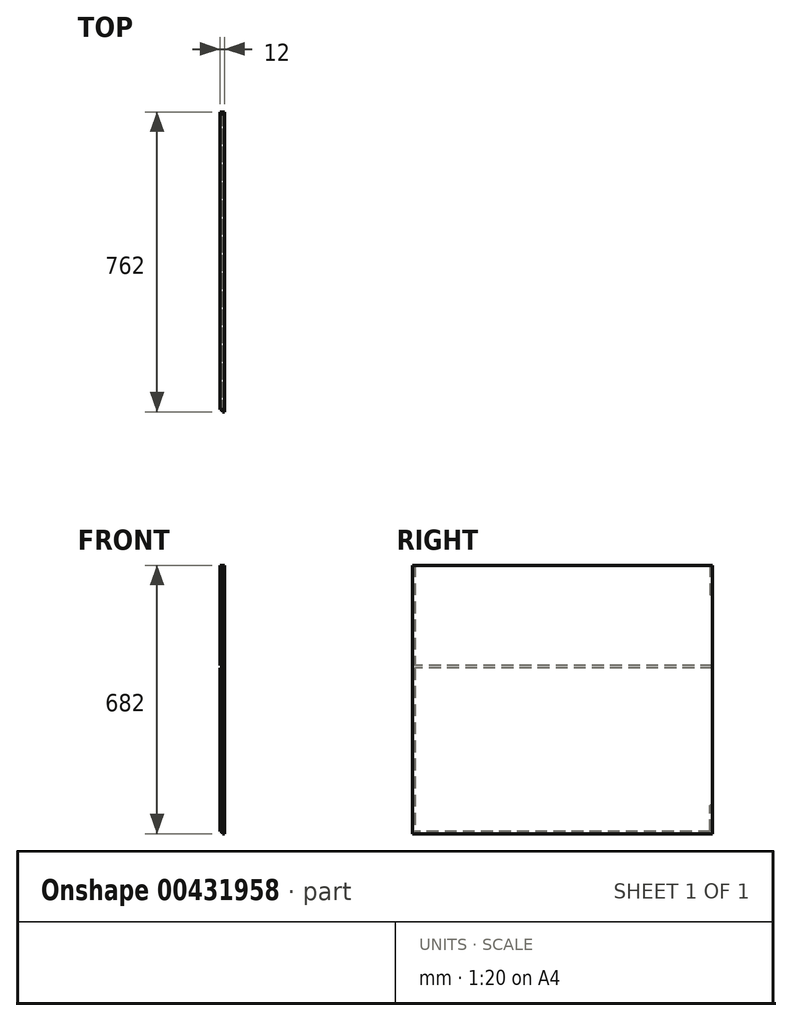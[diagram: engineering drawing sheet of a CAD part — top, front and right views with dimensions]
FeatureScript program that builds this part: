
annotation { "Feature Type Name" : "Feature", "Feature Type Description" : "" }
export const myFeature = defineFeature(function(context is Context, id is Id, definition is map)
    precondition{}
    {
        {
            var Q0;
            Q0=qCreatedBy(makeId("Right.planeOp"),FACE);
            var sketch = newSketch(context, id + "F0", { "sketchPlane" : qUnion([Q0])});
            skLineSegment(sketch, "E0.bottom", {"start": v(-381, 341) * mm, "end": v(381, 341) * mm});
            skLineSegment(sketch, "E0.top", {"start": v(-381, -341) * mm, "end": v(381, -341) * mm});
            skLineSegment(sketch, "E0.left", {"start": v(-381, 341) * mm, "end": v(-381, -341) * mm});
            skLineSegment(sketch, "E0.right", {"start": v(381, 341) * mm, "end": v(381, -341) * mm});
            skPoint(sketch, "E0.middle", {"position": v(0, 0) * mm});
            skSolve(sketch);
        }
        {
            var Q0;
            Q0=makeQuery(id+"F0.imprint","IMPRINT",FACE,{"disambiguationData":[TD([[makeQuery(id+"F0.imprint","IMPRINT",EDGE,{"derivedFrom":sQuery(id+"F0.wireOp",EDGE,"E0.bottom")}),-1.0]])]});
            extrude(context, id + "F1", {"entities" : qUnion([Q0]), "depth" : 12 * mm, "offsetDistance" : 25 * mm});
        }
        {
            var Q0;
            Q0=makeQuery(id+"F1.opExtrude","CAP_FACE",FACE,{"disambiguationData":[OSD([sQuery(id+"F0.wireOp",EDGE,"E0.bottom"),sQuery(id+"F0.wireOp",EDGE,"E0.top"),sQuery(id+"F0.wireOp",EDGE,"E0.left"),sQuery(id+"F0.wireOp",EDGE,"E0.right")])],"isStart":true});
            var sketch = newSketch(context, id + "F2", { "sketchPlane" : qUnion([Q0])});
            skLineSegment(sketch, "E1.bottom", {"start": v(381, 341) * mm, "end": v(375, 341) * mm});
            skLineSegment(sketch, "E1.top", {"start": v(381, -341) * mm, "end": v(375, -341) * mm});
            skLineSegment(sketch, "E1.left", {"start": v(381, 341) * mm, "end": v(381, -341) * mm});
            skLineSegment(sketch, "E1.right", {"start": v(375, 341) * mm, "end": v(375, -341) * mm});
            skSolve(sketch);
        }
        {
            var Q0;
            Q0=qSketchRegion(id+"F2",true);
            extrude(context, id + "F3", {"entities" : qUnion([Q0]), "operationType" : NewBodyOperationType.REMOVE, "oppositeDirection" : true, "depth" : 6 * mm, "offsetDistance" : 25 * mm});
        }
        {
            var Q0;
            {var subQ0=sQuery(id+"F0.wireOp",EDGE,"E0.bottom");var subQ1=sQuery(id+"F0.wireOp",EDGE,"E0.right");var subQ2=sQuery(id+"F0.wireOp",EDGE,"E0.top");Q0=makeQuery(id+"F3.boolean.opBoolean","SPLIT",FACE,{"disambiguationData":[TD([makeQuery(id+"F1.opExtrude","SWEPT_FACE",FACE,{"disambiguationData":[OSD([subQ1])]})])],"derivedFrom":makeQuery(id+"F1.opExtrude","CAP_FACE",FACE,{"disambiguationData":[OSD([subQ0,subQ2,sQuery(id+"F0.wireOp",EDGE,"E0.left"),subQ1])],"isStart":true})});}
            var sketch = newSketch(context, id + "F4", { "sketchPlane" : qUnion([Q0])});
            skLineSegment(sketch, "E2.bottom", {"start": v(-381, -335) * mm, "end": v(375, -335) * mm});
            skLineSegment(sketch, "E2.top", {"start": v(-381, -341) * mm, "end": v(375, -341) * mm});
            skLineSegment(sketch, "E2.left", {"start": v(-381, -335) * mm, "end": v(-381, -341) * mm});
            skLineSegment(sketch, "E2.right", {"start": v(375, -335) * mm, "end": v(375, -341) * mm});
            skSolve(sketch);
        }
        {
            var Q0;
            Q0=qSketchRegion(id+"F4",true);
            extrude(context, id + "F5", {"entities" : qUnion([Q0]), "operationType" : NewBodyOperationType.REMOVE, "oppositeDirection" : true, "depth" : 6 * mm, "offsetDistance" : 25 * mm});
        }
        {
            var Q0;
            {var subQ0=sQuery(id+"F0.wireOp",EDGE,"E0.bottom");var subQ1=sQuery(id+"F0.wireOp",EDGE,"E0.right");var subQ2=sQuery(id+"F0.wireOp",EDGE,"E0.top");Q0=makeQuery(id+"F3.boolean.opBoolean","SPLIT",FACE,{"disambiguationData":[TD([makeQuery(id+"F1.opExtrude","SWEPT_FACE",FACE,{"disambiguationData":[OSD([subQ1])]})])],"derivedFrom":makeQuery(id+"F1.opExtrude","CAP_FACE",FACE,{"disambiguationData":[OSD([subQ0,subQ2,sQuery(id+"F0.wireOp",EDGE,"E0.left"),subQ1])],"isStart":true})});}
            var sketch = newSketch(context, id + "F6", { "sketchPlane" : qUnion([Q0])});
            skLineSegment(sketch, "E3.bottom", {"start": v(-381, 341) * mm, "end": v(-375, 341) * mm});
            skLineSegment(sketch, "E3.top", {"start": v(-381, 266) * mm, "end": v(-375, 266) * mm});
            skLineSegment(sketch, "E3.left", {"start": v(-381, 341) * mm, "end": v(-381, 266) * mm});
            skLineSegment(sketch, "E3.right", {"start": v(-375, 341) * mm, "end": v(-375, 266) * mm});
            skSolve(sketch);
        }
        {
            var Q0;
            Q0=qSketchRegion(id+"F6",true);
            extrude(context, id + "F7", {"entities" : qUnion([Q0]), "operationType" : NewBodyOperationType.REMOVE, "oppositeDirection" : true, "depth" : 6 * mm, "offsetDistance" : 25 * mm});
        }
        {
            var Q0;
            {var subQ0=sQuery(id+"F0.wireOp",EDGE,"E0.bottom");var subQ1=sQuery(id+"F0.wireOp",EDGE,"E0.right");var subQ2=sQuery(id+"F0.wireOp",EDGE,"E0.top");Q0=makeQuery(id+"F3.boolean.opBoolean","SPLIT",FACE,{"disambiguationData":[TD([makeQuery(id+"F1.opExtrude","SWEPT_FACE",FACE,{"disambiguationData":[OSD([subQ1])]})])],"derivedFrom":makeQuery(id+"F1.opExtrude","CAP_FACE",FACE,{"disambiguationData":[OSD([subQ0,subQ2,sQuery(id+"F0.wireOp",EDGE,"E0.left"),subQ1])],"isStart":true})});}
            var sketch = newSketch(context, id + "F8", { "sketchPlane" : qUnion([Q0])});
            skLineSegment(sketch, "E4.bottom", {"start": v(-381, -335) * mm, "end": v(-375, -335) * mm});
            skLineSegment(sketch, "E4.top", {"start": v(-381, -269) * mm, "end": v(-375, -269) * mm});
            skLineSegment(sketch, "E4.left", {"start": v(-381, -335) * mm, "end": v(-381, -269) * mm});
            skLineSegment(sketch, "E4.right", {"start": v(-375, -335) * mm, "end": v(-375, -269) * mm});
            skSolve(sketch);
        }
        {
            var Q0;
            Q0=qSketchRegion(id+"F8",true);
            extrude(context, id + "F9", {"entities" : qUnion([Q0]), "operationType" : NewBodyOperationType.REMOVE, "oppositeDirection" : true, "depth" : 6 * mm, "offsetDistance" : 25 * mm});
        }
        {
            var Q0;
            Q0=makeQuery(id+"F1.opExtrude","CAP_FACE",FACE,{"disambiguationData":[OSD([sQuery(id+"F0.wireOp",EDGE,"E0.bottom"),sQuery(id+"F0.wireOp",EDGE,"E0.top"),sQuery(id+"F0.wireOp",EDGE,"E0.left"),sQuery(id+"F0.wireOp",EDGE,"E0.right")])],"isStart":true});
            var sketch = newSketch(context, id + "F10", { "sketchPlane" : qUnion([Q0])});
            skLineSegment(sketch, "E5.bottom", {"start": v(-381, 86) * mm, "end": v(375, 86) * mm});
            skLineSegment(sketch, "E5.top", {"start": v(-381, 80) * mm, "end": v(375, 80) * mm});
            skLineSegment(sketch, "E5.left", {"start": v(-381, 86) * mm, "end": v(-381, 80) * mm});
            skLineSegment(sketch, "E5.right", {"start": v(375, 86) * mm, "end": v(375, 80) * mm});
            skSolve(sketch);
        }
        {
            var Q0;
            Q0 = qSketchRegion(id + "F10", true);
            extrude(context, id + "F11", {"entities" : qUnion([Q0]), "operationType" : NewBodyOperationType.REMOVE, "oppositeDirection" : true, "depth" : 6 * mm, "offsetDistance" : 25 * mm});
        }
    });
